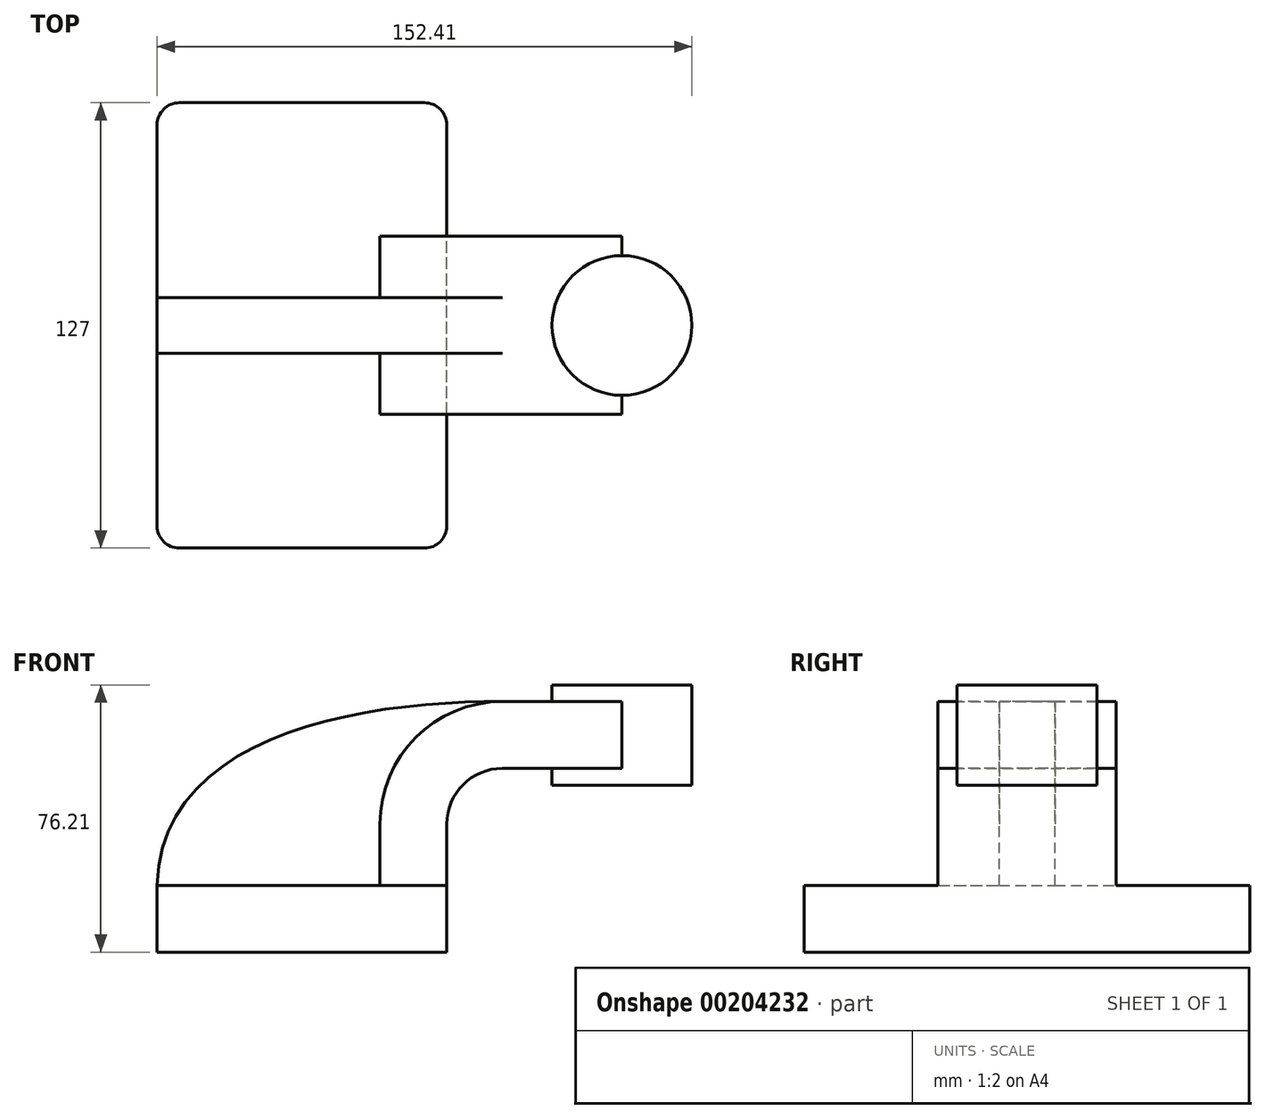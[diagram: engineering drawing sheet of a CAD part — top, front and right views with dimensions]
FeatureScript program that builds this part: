
annotation { "Feature Type Name" : "Feature", "Feature Type Description" : "" }
export const myFeature = defineFeature(function(context is Context, id is Id, definition is map)
    precondition{}
    {
        {
            var Q0;
            Q0=qCreatedBy(makeId("Front.planeOp"),FACE);
            var sketch = newSketch(context, id + "F0", { "sketchPlane" : qUnion([Q0])});
            skLineSegment(sketch, "E0.bottom", {"start": v(41.27, 9.53) * mm, "end": v(-41.28, 9.53) * mm});
            skLineSegment(sketch, "E0.top", {"start": v(41.28, -9.52) * mm, "end": v(-41.27, -9.52) * mm});
            skLineSegment(sketch, "E0.left", {"start": v(41.28, 9.53) * mm, "end": v(41.28, -9.52) * mm});
            skLineSegment(sketch, "E0.right", {"start": v(-41.28, 9.53) * mm, "end": v(-41.27, -9.52) * mm});
            skPoint(sketch, "E0.middle", {"position": v(0, 0) * mm});
            skLineSegment(sketch, "E1.bottom", {"start": v(60.32, 38.1) * mm, "end": v(111.12, 38.1) * mm});
            skLineSegment(sketch, "E1.top", {"start": v(60.32, 66.68) * mm, "end": v(111.12, 66.68) * mm});
            skLineSegment(sketch, "E1.left", {"start": v(60.32, 38.1) * mm, "end": v(60.32, 66.68) * mm});
            skLineSegment(sketch, "E1.right", {"start": v(111.12, 38.1) * mm, "end": v(111.12, 66.68) * mm});
            skPoint(sketch, "E1.middle", {"position": v(85.72, 52.39) * mm});
            skLineSegment(sketch, "E2", {"start": v(41.27, 9.53) * mm, "end": v(41.27, 27) * mm});
            skArc(sketch, "E3", {"start": v(57.15, 42.88) * mm, "mid": v(45.92, 38.23) * mm, "end": v(41.27, 27) * mm});
            skLineSegment(sketch, "E4", {"start": v(57.15, 42.88) * mm, "end": v(91.2, 42.88) * mm});
            skLineSegment(sketch, "E5.0", {"start": v(57.15, 61.93) * mm, "end": v(91.2, 61.93) * mm});
            skArc(sketch, "E5.1", {"start": v(57.15, 61.93) * mm, "mid": v(32.45, 51.7) * mm, "end": v(22.23, 27) * mm});
            skLineSegment(sketch, "E5.2", {"start": v(22.22, 9.53) * mm, "end": v(22.22, 27) * mm});
            skLineSegment(sketch, "E6", {"start": v(91.2, 38.1) * mm, "end": v(91.2, 66.68) * mm});
            skFitSpline(sketch, "E7", {"points": [v(-41.28, 9.52) * mm, v(57.15, 61.93) * mm], "startDerivative": vector(3.7, 130.3) * mm, "endDerivative": vector(119.04, -0.4) * mm});
            skSolve(sketch);
        }
        {
            var Q0;
            Q0=makeQuery(id+"F0.imprint","IMPRINT",FACE,{"disambiguationData":[TD([[makeQuery(id+"F0.imprint","IMPRINT",EDGE,{"derivedFrom":sQuery(id+"F0.wireOp",EDGE,"E0.top")}),-1.0]])]});
            extrude(context, id + "F1", {"entities" : qUnion([Q0]), "endBound" : BoundingType.SYMMETRIC, "depth" : 127 * mm});
        }
        {
            var Q0;
            {var subQ1=sQuery(id+"F0.wireOp",EDGE,"E2");Q0=makeQuery(id+"F0.imprint","IMPRINT",FACE,{"disambiguationData":[TD([[makeQuery(id+"F0.imprint","IMPRINT",EDGE,{"derivedFrom":subQ1}),1.0]])]});}
            var Q1;
            {var subQ0=sQuery(id+"F0.wireOp",EDGE,"E4");var subQ1=sQuery(id+"F0.wireOp",EDGE,"E1.left");var subQ2=makeQuery(id+"F0.imprint","INTERSECT",VERTEX,{"derivedFrom":[subQ1,subQ0]});Q1=makeQuery(id+"F0.imprint","IMPRINT",FACE,{"disambiguationData":[TD([[makeQuery(id+"F0.imprint","IMPRINT",EDGE,{"disambiguationData":[TD([[subQ2,-1.0]])],"derivedFrom":subQ1}),-1.0]])]});}
            extrude(context, id + "F2", {"entities" : qUnion([Q0, Q1]), "operationType" : NewBodyOperationType.ADD, "endBound" : BoundingType.SYMMETRIC, "depth" : 50.8 * mm});
        }
        {
            var Q0;
            Q0=makeQuery(id+"F0.imprint","IMPRINT",FACE,{"disambiguationData":[TD([[makeQuery(id+"F0.imprint","IMPRINT",EDGE,{"derivedFrom":sQuery(id+"F0.wireOp",EDGE,"E5.1")}),-1.0]])]});
            extrude(context, id + "F3", {"entities" : qUnion([Q0]), "operationType" : NewBodyOperationType.ADD, "endBound" : BoundingType.SYMMETRIC, "depth" : 15.88 * mm});
        }
        {
            var Q0;
            {var subQ0=sQuery(id+"F0.wireOp",EDGE,"E1.right");Q0=makeQuery(id+"F0.imprint","IMPRINT",FACE,{"disambiguationData":[TD([[makeQuery(id+"F0.imprint","IMPRINT",EDGE,{"derivedFrom":subQ0}),1.0]])]});}
            var Q1;
            Q1=sQuery(id+"F0.wireOp",EDGE,"E6");
            revolve(context, id + "F4", {"operationType" : NewBodyOperationType.ADD, "entities" : qUnion([Q0]), "axis" : qUnion([Q1]), "revolveType" : RevolveType.FULL});
        }
        {
            var Q0;
            Q0=makeQuery(id+"F1.opExtrude","CAP_EDGE",EDGE,{"disambiguationData":[OSD([sQuery(id+"F0.wireOp",EDGE,"E0.left")])],"isStart":false});
            var Q1;
            Q1=makeQuery(id+"F1.opExtrude","CAP_EDGE",EDGE,{"disambiguationData":[OSD([sQuery(id+"F0.wireOp",EDGE,"E0.left")])],"isStart":true});
            var Q2;
            Q2=makeQuery(id+"F1.opExtrude","CAP_EDGE",EDGE,{"disambiguationData":[OSD([sQuery(id+"F0.wireOp",EDGE,"E0.right")])],"isStart":true});
            var Q3;
            Q3=makeQuery(id+"F1.opExtrude","CAP_EDGE",EDGE,{"disambiguationData":[OSD([sQuery(id+"F0.wireOp",EDGE,"E0.right")])],"isStart":false});
            fillet(context, id + "F5", {"entities" : qUnion([Q0, Q1, Q2, Q3]), "radius" : 6.35 * mm, "tangentPropagation" : true, "allowEdgeOverflow" : false});
        }
    });
